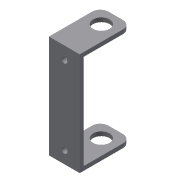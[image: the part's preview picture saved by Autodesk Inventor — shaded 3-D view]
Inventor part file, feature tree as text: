
AUTODESK INVENTOR PART (.ipt)
format: ipt  version: 2015 (Build 190159000, 159)  size: 115,712 bytes
history: native  units: mm
features: extrude x3, sketch x2, fillet x1
ambient origin geometry x8: Origin, YZ Plane, XZ Plane, XY Plane, X Axis, Y Axis, Z Axis, Center Point
bodies: Solid1 (feature_tree)
feature tree (6):
  sketch  "Sketch1"  dims[d0=15.0mm d1=50.0mm]
  extrude  "Extrusion1"  Depth=50.0mm
  extrude  "Extrusion2"  Depth=4.0mm
  extrude  "Extrusion3"  Depth=4.0mm
  fillet  "Fillet1"  Radius=3.0mm
  sketch  "Sketch2"  dims[d2=1.0mm d3=38.0mm d4=3.0mm d5=3.0mm d6=15.0mm d7=2.0mm d8=15.0mm d9=2.0mm d10=2.0mm d11=0.0mm d12=25.0mm d13=0.0mm d14=18.0mm d15=90.0deg d16=8.0mm d17=50.0mm d18=0.0mm d19=4.0mm]
